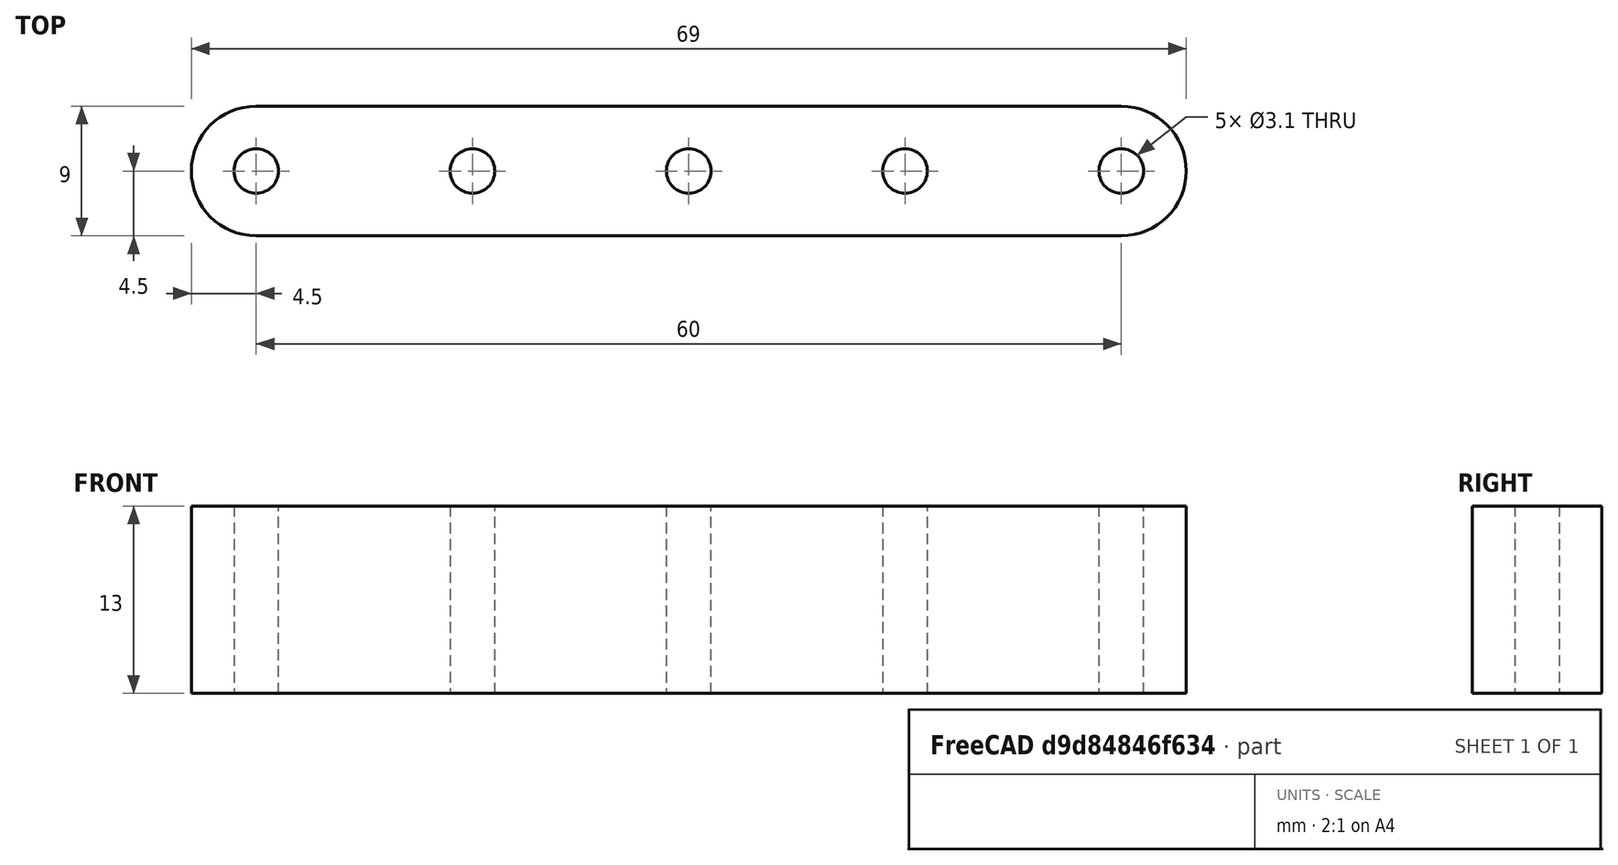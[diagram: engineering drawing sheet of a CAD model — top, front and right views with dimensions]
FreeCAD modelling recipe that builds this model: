
FCSTD DOCUMENT  (FreeCAD 0.21R33771 (Git))
Label: haste-articulada
License: All rights reserved
LicenseURL: https://en.wikipedia.org/wiki/All_rights_reserved
objects: Sketcher::SketchObject×1, PartDesign::Pad×1, PartDesign::Body×1
note: 4 computed .brp shape members not serialized (recipe doc carries the construction recipe); baked Part::Feature solids carry a one-line shape summary decoded from their .brp

FEATURE [Sketcher::SketchObject] Sketch
  FullyConstrained = true
  MapMode = 5
  Support = -> [XY_Plane]
  sketch-geometry (10):
    g0: ArcOfCircle CenterX=-30 CenterY=0 CenterZ=0 NormalX=0 NormalY=0 NormalZ=1 AngleXU=0 Radius=4.5 StartAngle=1.5708 EndAngle=4.71239
    g1: ArcOfCircle CenterX=30 CenterY=-3e-16 CenterZ=0 NormalX=0 NormalY=0 NormalZ=1 AngleXU=0 Radius=4.5 StartAngle=4.71239 EndAngle=7.85398
    g2: LineSegment StartX=-30 StartY=-4.5 StartZ=0 EndX=30 EndY=-4.5 EndZ=0
    g3: LineSegment StartX=30 StartY=4.5 StartZ=0 EndX=-30 EndY=4.5 EndZ=0
    g4: Circle CenterX=-30 CenterY=0 CenterZ=0 NormalX=0 NormalY=0 NormalZ=1 AngleXU=0 Radius=1.55
    g5: Circle CenterX=30 CenterY=-3e-16 CenterZ=0 NormalX=0 NormalY=0 NormalZ=1 AngleXU=0 Radius=1.55
    g6: Circle CenterX=0 CenterY=0 CenterZ=0 NormalX=0 NormalY=0 NormalZ=1 AngleXU=0 Radius=1.55
    g7: Circle CenterX=-15 CenterY=0 CenterZ=0 NormalX=0 NormalY=0 NormalZ=1 AngleXU=0 Radius=1.55
    g8: Circle CenterX=15 CenterY=0 CenterZ=0 NormalX=0 NormalY=0 NormalZ=1 AngleXU=0 Radius=1.55
    g9: LineSegment StartX=-15 StartY=4.5 StartZ=0 EndX=-15 EndY=-4.5 EndZ=0
  constraints (23):
    c: Tangent(g0,g2) = -1.5708
    c: Tangent(g2,g1) = -1.5708
    c: Tangent(g1,g3) = -1.5708
    c: Tangent(g3,g0) = -1.5708
    c: Equal(g0,g1)
    c: Symmetric(g0,g1,g-2)
    c: PointOnObject(g0,g-1)
    c: Radius(g1) = 4.5
    c: DistanceX(g0,g1) = 60
    c: Coincident(g4,g0)
    c: Coincident(g5,g1)
    c: Equal(g5,g4)
    c: Diameter(g5) = 3.1
    c: Coincident(g6,g-1)
    c: PointOnObject(g7,g-1)
    c: Symmetric(g8,g7,g-2)
    c: Equal(g7,g6)
    c: Equal(g6,g8)
    c: Equal(g8,g4)
    c: Symmetric(g6,g0,g9)
    c: PointOnObject(g7,g9)
    c: PointOnObject(g9,g3)
    c: PointOnObject(g9,g2)
FEATURE [PartDesign::Pad] Pad
  Direction = (0,0,1)
  Length = 13
  Length2 = 10
  Profile = -> Sketch
  ReferenceAxis = -> Sketch [N_Axis]
  Type = 0
FEATURE [PartDesign::Body] Body
  Group = -> [Sketch,Pad]
  Origin = -> Origin
  Tip = -> Pad
